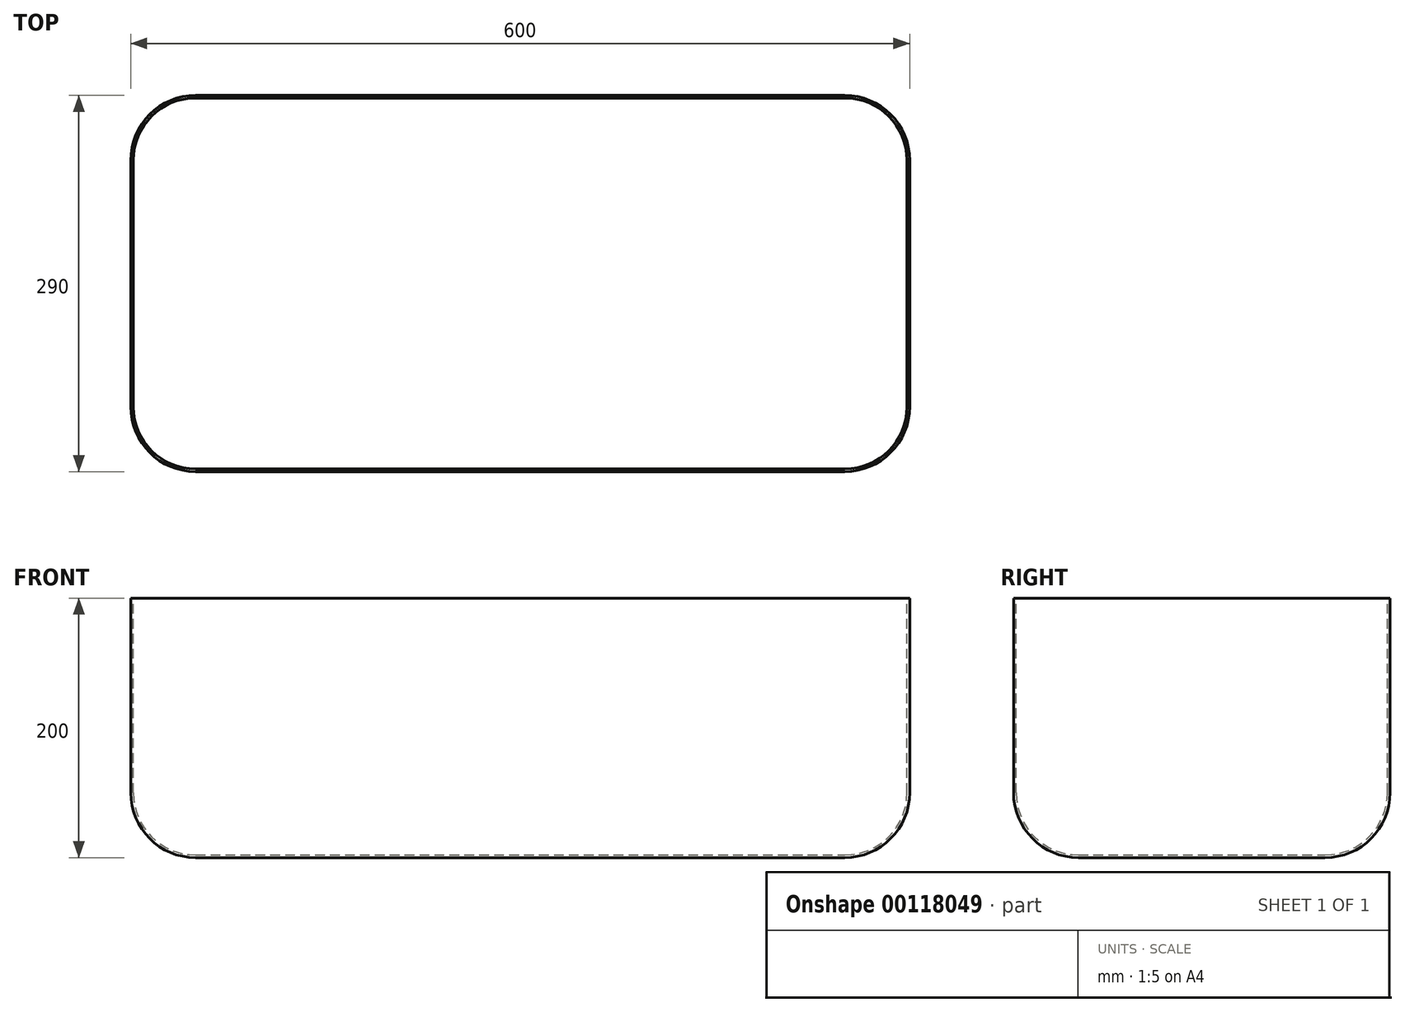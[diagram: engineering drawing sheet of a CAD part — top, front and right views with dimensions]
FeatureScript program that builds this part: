
annotation { "Feature Type Name" : "Feature", "Feature Type Description" : "" }
export const myFeature = defineFeature(function(context is Context, id is Id, definition is map)
    precondition{}
    {
        {
            var Q0;
            Q0=qCreatedBy(makeId("Front.planeOp"),FACE);
            var sketch = newSketch(context, id + "F0", { "sketchPlane" : qUnion([Q0])});
            skLineSegment(sketch, "E0.bottom", {"start": v(0, 0) * mm, "end": v(600, 0) * mm});
            skLineSegment(sketch, "E0.top", {"start": v(0, 200) * mm, "end": v(600, 200) * mm});
            skLineSegment(sketch, "E0.left", {"start": v(0, 0) * mm, "end": v(0, 200) * mm});
            skLineSegment(sketch, "E0.right", {"start": v(600, 0) * mm, "end": v(600, 200) * mm});
            skSolve(sketch);
        }
        {
            var Q0;
            Q0 = qSketchRegion(id + "F0", true);
            extrude(context, id + "F1", {"entities" : qUnion([Q0]), "depth" : 290 * mm});
        }
        {
            var Q0;
            Q0=makeQuery(id+"F1.opExtrude","CAP_EDGE",EDGE,{"disambiguationData":[OSD([sQuery(id+"F0.wireOp",EDGE,"E0.right")])],"isStart":false});
            var Q1;
            Q1=makeQuery(id+"F1.opExtrude","CAP_EDGE",EDGE,{"disambiguationData":[OSD([sQuery(id+"F0.wireOp",EDGE,"E0.left")])],"isStart":false});
            var Q2;
            Q2=makeQuery(id+"F1.opExtrude","CAP_EDGE",EDGE,{"disambiguationData":[OSD([sQuery(id+"F0.wireOp",EDGE,"E0.right")])],"isStart":true});
            var Q3;
            Q3=makeQuery(id+"F1.opExtrude","SWEPT_EDGE",EDGE,{"disambiguationData":[OSD([sQuery(id+"F0.wireOp",EDGE,"E0.bottom"),sQuery(id+"F0.wireOp",EDGE,"E0.right")])]});
            var Q4;
            Q4=makeQuery(id+"F1.opExtrude","CAP_EDGE",EDGE,{"disambiguationData":[OSD([sQuery(id+"F0.wireOp",EDGE,"E0.bottom")])],"isStart":false});
            var Q5;
            Q5=makeQuery(id+"F1.opExtrude","SWEPT_EDGE",EDGE,{"disambiguationData":[OSD([sQuery(id+"F0.wireOp",EDGE,"E0.bottom"),sQuery(id+"F0.wireOp",EDGE,"E0.left")])]});
            var Q6;
            Q6=makeQuery(id+"F1.opExtrude","CAP_EDGE",EDGE,{"disambiguationData":[OSD([sQuery(id+"F0.wireOp",EDGE,"E0.left")])],"isStart":true});
            var Q7;
            Q7=makeQuery(id+"F1.opExtrude","CAP_EDGE",EDGE,{"disambiguationData":[OSD([sQuery(id+"F0.wireOp",EDGE,"E0.bottom")])],"isStart":true});
            fillet(context, id + "F2", {"entities" : qUnion([Q0, Q1, Q2, Q3, Q4, Q5, Q6, Q7]), "radius" : 50 * mm, "tangentPropagation" : true, "allowEdgeOverflow" : false});
        }
        {
            var Q0;
            Q0=makeQuery(id+"F1.opExtrude","SWEPT_FACE",FACE,{"disambiguationData":[OSD([sQuery(id+"F0.wireOp",EDGE,"E0.top")])]});
            shell(context, id + "F3", {"entities" : qUnion([Q0]), "thickness" : 2 * mm});
        }
    });
